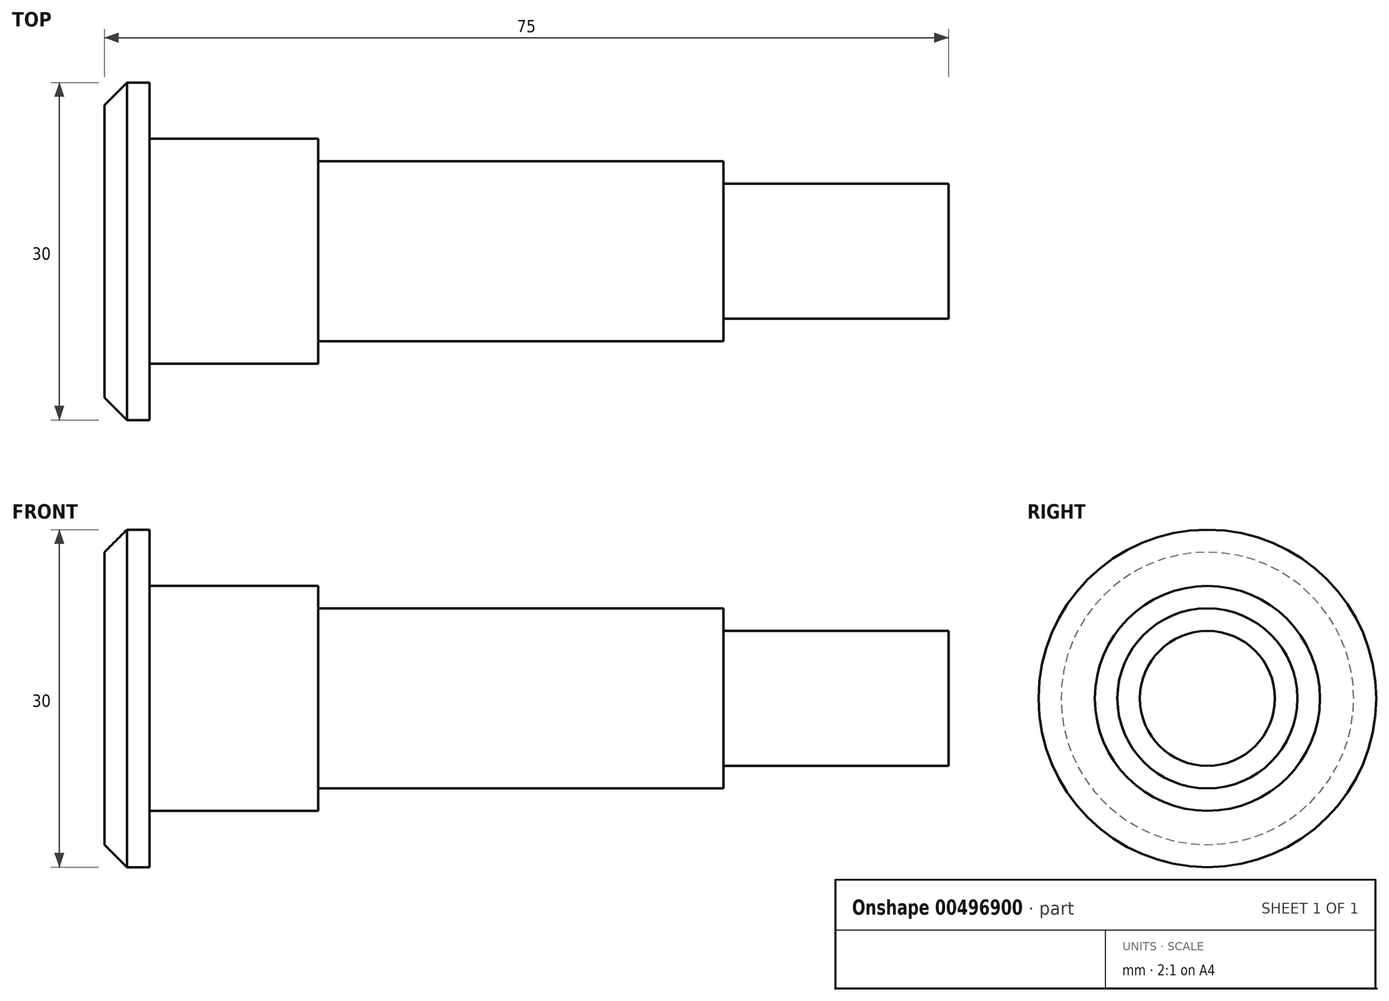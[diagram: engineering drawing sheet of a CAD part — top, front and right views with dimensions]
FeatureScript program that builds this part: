
annotation { "Feature Type Name" : "Feature", "Feature Type Description" : "" }
export const myFeature = defineFeature(function(context is Context, id is Id, definition is map)
    precondition{}
    {
        {
            var Q0;
            Q0=qCreatedBy(makeId("Front.planeOp"),FACE);
            var sketch = newSketch(context, id + "F0", { "sketchPlane" : qUnion([Q0])});
            skLineSegment(sketch, "E0", {"start": v(-59.18, 0) * mm, "end": v(-59.18, 15) * mm});
            skLineSegment(sketch, "E1", {"start": v(-59.18, 15) * mm, "end": v(-55.18, 15) * mm});
            skLineSegment(sketch, "E2", {"start": v(-55.18, 15) * mm, "end": v(-55.18, 0) * mm});
            skLineSegment(sketch, "E3", {"start": v(-55.18, 0) * mm, "end": v(-55.18, 10) * mm});
            skLineSegment(sketch, "E4", {"start": v(-55.18, 10) * mm, "end": v(-40.18, 10) * mm});
            skLineSegment(sketch, "E5", {"start": v(-40.18, 10) * mm, "end": v(-40.18, 0) * mm});
            skLineSegment(sketch, "E6", {"start": v(-40.18, 0) * mm, "end": v(-40.18, 8) * mm});
            skLineSegment(sketch, "E7", {"start": v(-40.18, 8) * mm, "end": v(-4.18, 8) * mm});
            skLineSegment(sketch, "E8", {"start": v(-4.18, 8) * mm, "end": v(-4.18, 0) * mm});
            skLineSegment(sketch, "E9", {"start": v(-4.18, 0) * mm, "end": v(-4.18, 6) * mm});
            skLineSegment(sketch, "E10", {"start": v(-4.18, 6) * mm, "end": v(15.82, 6) * mm});
            skLineSegment(sketch, "E11", {"start": v(15.82, 6) * mm, "end": v(15.82, 0) * mm});
            skLineSegment(sketch, "E12", {"start": v(15.82, 0) * mm, "end": v(15.82, 4) * mm});
            skLineSegment(sketch, "E13", {"start": v(-59.18, 0) * mm, "end": v(15.82, 0) * mm});
            skSolve(sketch);
        }
        {
            var Q0;
            Q0 = qSketchRegion(id + "F0", true);
            var Q1;
            Q1=sQuery(id+"F0.wireOp",EDGE,"E13");
            revolve(context, id + "F1", {"entities" : qUnion([Q0]), "axis" : qUnion([Q1]), "revolveType" : RevolveType.FULL});
        }
        {
            var Q0;
            Q0=makeQuery(id+"F1.opRevolve","SWEPT_EDGE",EDGE,{"disambiguationData":[OSD([sQuery(id+"F0.wireOp",EDGE,"E0"),sQuery(id+"F0.wireOp",EDGE,"E1")])]});
            chamfer(context, id + "F2", {"entities" : qUnion([Q0]), "width" : 2 * mm, "tangentPropagation" : true});
        }
    });
